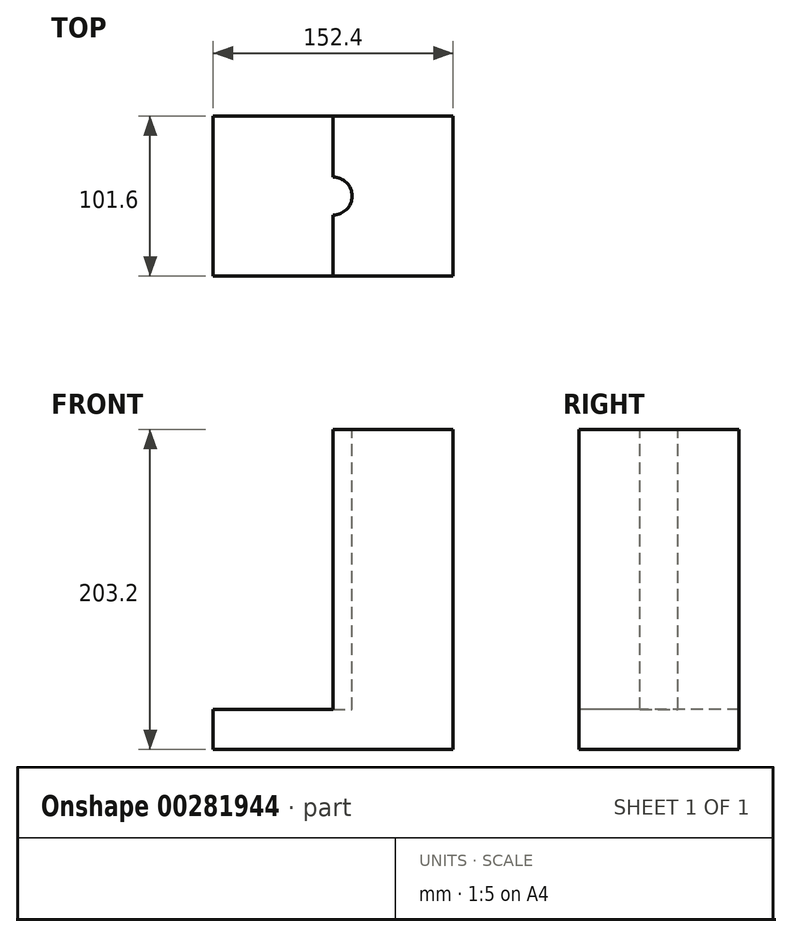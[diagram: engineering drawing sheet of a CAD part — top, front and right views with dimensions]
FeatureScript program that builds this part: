
annotation { "Feature Type Name" : "Feature", "Feature Type Description" : "" }
export const myFeature = defineFeature(function(context is Context, id is Id, definition is map)
    precondition{}
    {
        {
            var Q0;
            Q0=qCreatedBy(makeId("Top.planeOp"),FACE);
            var sketch = newSketch(context, id + "F0", { "sketchPlane" : qUnion([Q0])});
            skLineSegment(sketch, "E0.bottom", {"start": v(-70.96, 61.6) * mm, "end": v(81.44, 61.6) * mm});
            skLineSegment(sketch, "E0.top", {"start": v(-70.96, -40) * mm, "end": v(81.44, -40) * mm});
            skLineSegment(sketch, "E0.left", {"start": v(-70.96, 61.6) * mm, "end": v(-70.96, -40) * mm});
            skLineSegment(sketch, "E0.right", {"start": v(81.44, 61.6) * mm, "end": v(81.44, -40) * mm});
            skSolve(sketch);
        }
        {
            var Q0;
            Q0 = qSketchRegion(id + "F0", true);
            extrude(context, id + "F1", {"entities" : qUnion([Q0]), "depth" : 25.4 * mm, "offsetDistance" : 25.4 * mm});
        }
        {
            var Q0;
            Q0=makeQuery(id+"F1.opExtrude","CAP_FACE",FACE,{"disambiguationData":[OSD([sQuery(id+"F0.wireOp",EDGE,"E0.bottom"),sQuery(id+"F0.wireOp",EDGE,"E0.top"),sQuery(id+"F0.wireOp",EDGE,"E0.left"),sQuery(id+"F0.wireOp",EDGE,"E0.right")])],"isStart":false});
            var sketch = newSketch(context, id + "F2", { "sketchPlane" : qUnion([Q0])});
            skLineSegment(sketch, "E1.bottom", {"start": v(5.24, 61.6) * mm, "end": v(81.44, 61.6) * mm});
            skLineSegment(sketch, "E1.top", {"start": v(5.24, -40) * mm, "end": v(81.44, -40) * mm});
            skLineSegment(sketch, "E1.left", {"start": v(5.24, 61.6) * mm, "end": v(5.24, -40) * mm});
            skLineSegment(sketch, "E1.right", {"start": v(81.44, 61.6) * mm, "end": v(81.44, -40) * mm});
            skSolve(sketch);
        }
        {
            var Q0;
            Q0 = qSketchRegion(id + "F2", true);
            extrude(context, id + "F3", {"entities" : qUnion([Q0]), "operationType" : NewBodyOperationType.ADD, "depth" : 177.8 * mm, "offsetDistance" : 25.4 * mm});
        }
        {
            var Q0;
            Q0=makeQuery(id+"F3.opExtrude","CAP_FACE",FACE,{"disambiguationData":[OSD([sQuery(id+"F2.wireOp",EDGE,"E1.bottom"),sQuery(id+"F2.wireOp",EDGE,"E1.top"),sQuery(id+"F2.wireOp",EDGE,"E1.left"),sQuery(id+"F2.wireOp",EDGE,"E1.right")])],"isStart":false});
            var sketch = newSketch(context, id + "F4", { "sketchPlane" : qUnion([Q0])});
            skCircle(sketch, "E2", {"center": v(5.24, 10.8) * mm, "radius": 12.07 * mm});
            skSolve(sketch);
        }
        {
            var Q0;
            Q0 = qSketchRegion(id + "F4", true);
            extrude(context, id + "F5", {"entities" : qUnion([Q0]), "operationType" : NewBodyOperationType.REMOVE, "oppositeDirection" : true, "depth" : 177.8 * mm, "offsetDistance" : 25.4 * mm});
        }
    });
